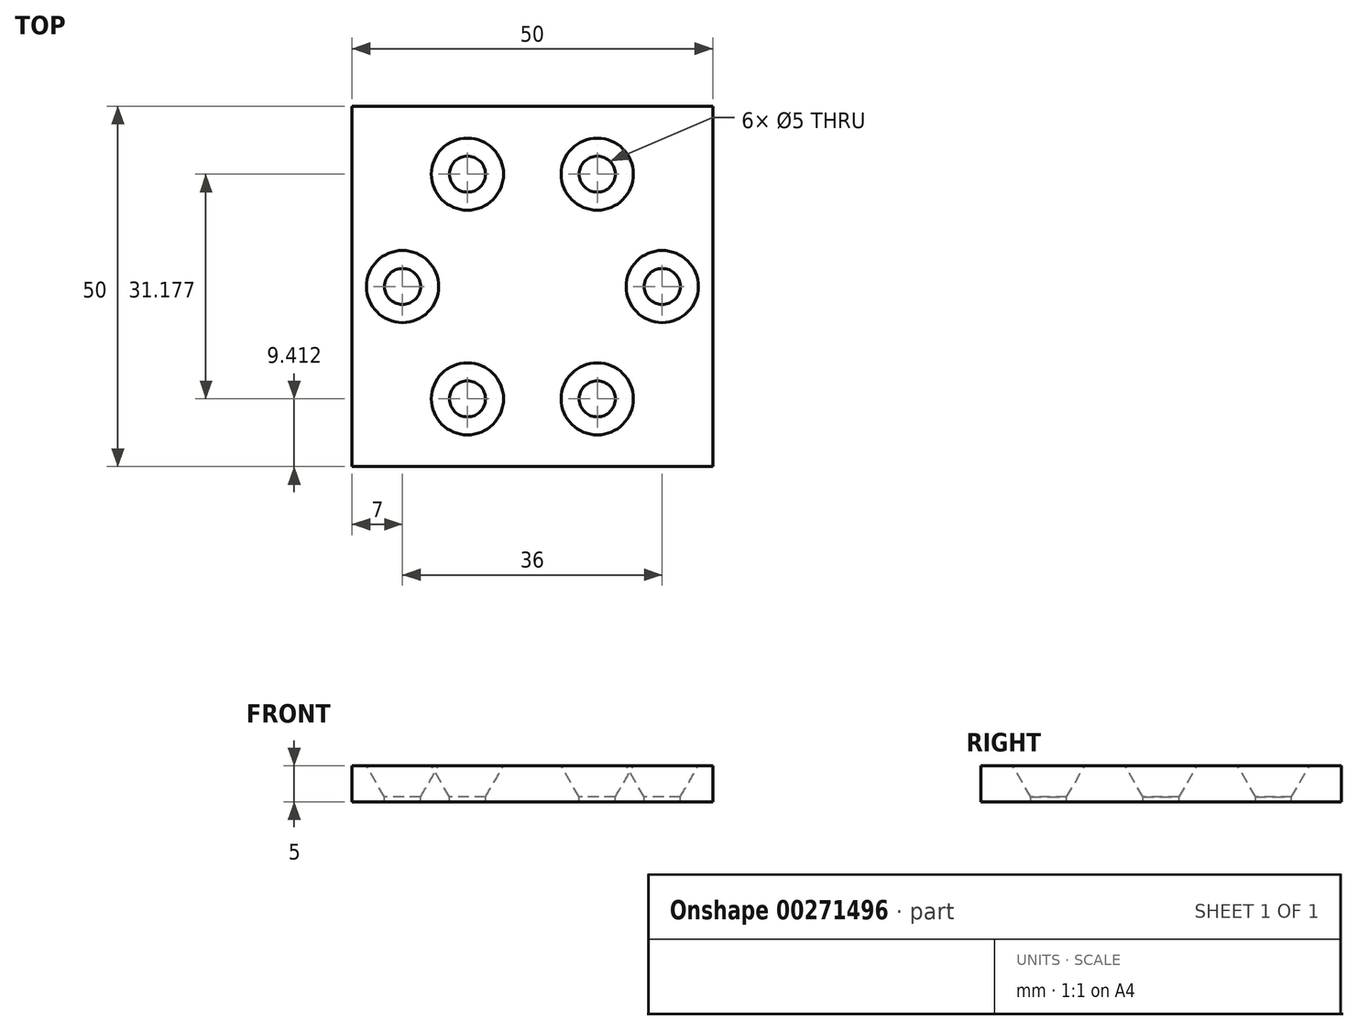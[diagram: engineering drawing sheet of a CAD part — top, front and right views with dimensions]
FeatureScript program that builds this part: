
annotation { "Feature Type Name" : "Feature", "Feature Type Description" : "" }
export const myFeature = defineFeature(function(context is Context, id is Id, definition is map)
    precondition{}
    {
        {
            var Q0;
            Q0=qCreatedBy(makeId("Top.planeOp"),FACE);
            var sketch = newSketch(context, id + "F0", { "sketchPlane" : qUnion([Q0])});
            skLineSegment(sketch, "E0.bottom", {"start": v(-25, 25) * mm, "end": v(25, 25) * mm});
            skLineSegment(sketch, "E0.top", {"start": v(-25, -25) * mm, "end": v(25, -25) * mm});
            skLineSegment(sketch, "E0.left", {"start": v(-25, 25) * mm, "end": v(-25, -25) * mm});
            skLineSegment(sketch, "E0.right", {"start": v(25, 25) * mm, "end": v(25, -25) * mm});
            skPoint(sketch, "E0.middle", {"position": v(0, 0) * mm});
            skSolve(sketch);
        }
        {
            var Q0;
            Q0=makeQuery(id+"F0.imprint","IMPRINT",FACE,{"disambiguationData":[TD([[makeQuery(id+"F0.imprint","IMPRINT",EDGE,{"derivedFrom":sQuery(id+"F0.wireOp",EDGE,"E0.bottom")}),-1.0]])]});
            extrude(context, id + "F1", {"entities" : qUnion([Q0]), "depth" : 5 * mm});
        }
        {
            var Q0;
            Q0=makeQuery(id+"F1.opExtrude","CAP_FACE",FACE,{"disambiguationData":[OSD([sQuery(id+"F0.wireOp",EDGE,"E0.bottom"),sQuery(id+"F0.wireOp",EDGE,"E0.top"),sQuery(id+"F0.wireOp",EDGE,"E0.left"),sQuery(id+"F0.wireOp",EDGE,"E0.right")])],"isStart":false});
            var sketch = newSketch(context, id + "F2", { "sketchPlane" : qUnion([Q0])});
            skCircle(sketch, "E1.cCircle", {"center": v(0, 0) * mm, "radius": 15.59 * mm, "construction": true});
            skLineSegment(sketch, "E1.0", {"start": v(-9, 15.59) * mm, "end": v(9, 15.59) * mm});
            skLineSegment(sketch, "E1.1", {"start": v(9, 15.59) * mm, "end": v(18, 0) * mm});
            skLineSegment(sketch, "E1.2", {"start": v(18, 0) * mm, "end": v(9, -15.59) * mm});
            skLineSegment(sketch, "E1.3", {"start": v(9, -15.59) * mm, "end": v(-9, -15.59) * mm});
            skLineSegment(sketch, "E1.4", {"start": v(-9, -15.59) * mm, "end": v(-18, 0) * mm});
            skLineSegment(sketch, "E1.5", {"start": v(-18, 0) * mm, "end": v(-9, 15.59) * mm});
            skPoint(sketch, "E1.0.midPoint", {"position": v(0, 15.59) * mm});
            skSolve(sketch);
        }
        {
            var Q0;
            Q0=sQuery(id+"F2.wireOp",VERTEX,"E1.1.start");
            var Q1;
            Q1=sQuery(id+"F2.wireOp",VERTEX,"E1.2.start");
            var Q2;
            Q2=sQuery(id+"F2.wireOp",VERTEX,"E1.3.start");
            var Q3;
            Q3=sQuery(id+"F2.wireOp",VERTEX,"E1.4.start");
            var Q4;
            Q4=sQuery(id+"F2.wireOp",VERTEX,"E1.5.start");
            var Q5;
            Q5=sQuery(id+"F2.wireOp",VERTEX,"E1.0.start");
            var Q6;
            Q6=makeQuery(id+"F1.opExtrude","SWEPT_BODY",BODY,{"disambiguationData":[OSD([sQuery(id+"F0.wireOp",EDGE,"E0.bottom"),sQuery(id+"F0.wireOp",EDGE,"E0.top"),sQuery(id+"F0.wireOp",EDGE,"E0.left"),sQuery(id+"F0.wireOp",EDGE,"E0.right")])]});
            hole(context, id + "F3", {"style" : HoleStyle.C_SINK, "endStyle" : HoleEndStyle.BLIND, "holeDiameter" : 5 * mm, "cSinkDiameter" : 10 * mm, "cSinkAngle" : 60 * degree, "holeDepth" : 12 * mm, "tappedDepth" : 12 * mm, "tapClearance" : 3, "locations" : qUnion([Q0, Q1, Q2, Q3, Q4, Q5]), "scope" : qUnion([Q6])});
        }
    });
